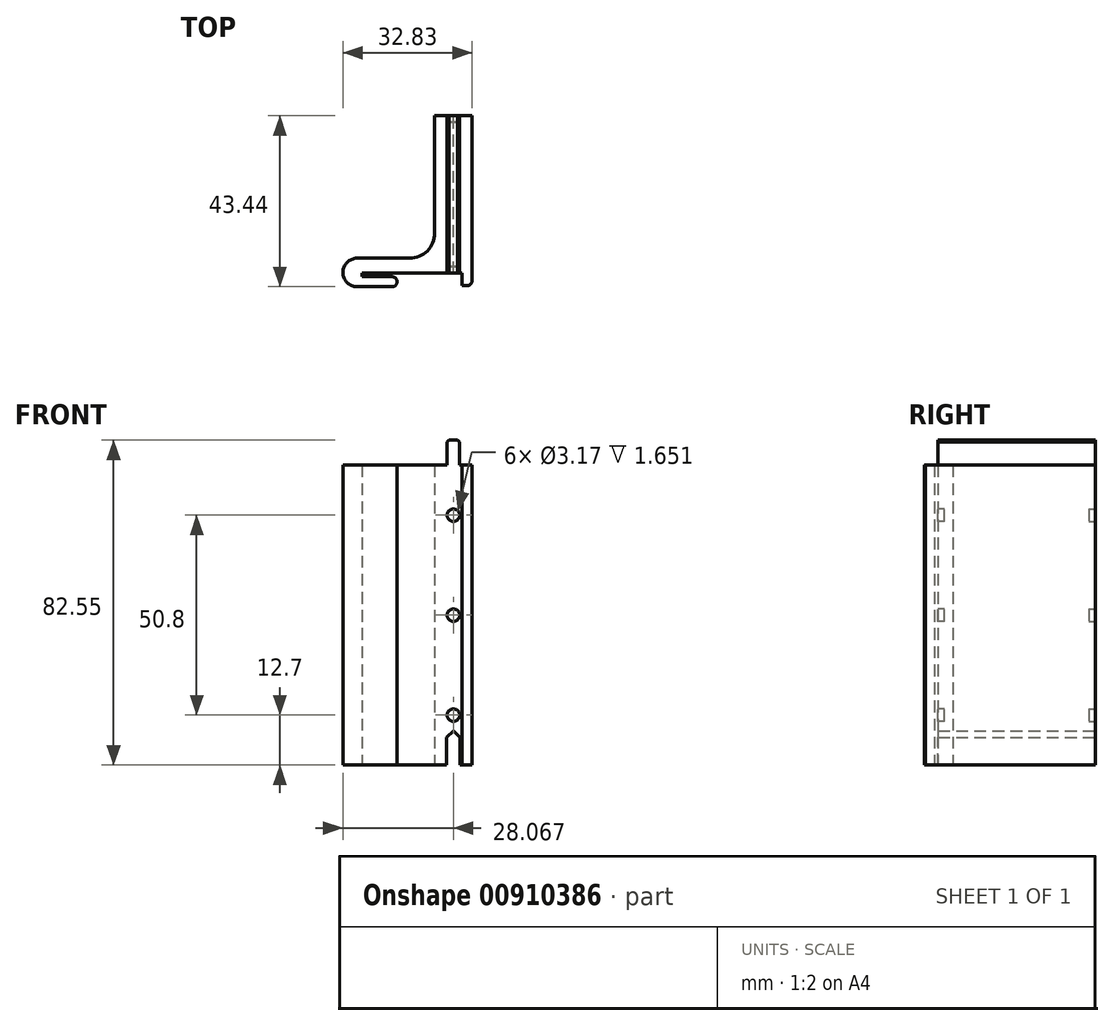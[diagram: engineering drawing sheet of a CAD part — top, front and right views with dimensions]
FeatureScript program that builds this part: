
annotation { "Feature Type Name" : "Feature", "Feature Type Description" : "" }
export const myFeature = defineFeature(function(context is Context, id is Id, definition is map)
    precondition{}
    {
        {
            var Q0;
            Q0=qCreatedBy(makeId("Top.planeOp"),FACE);
            var sketch = newSketch(context, id + "F0", { "sketchPlane" : qUnion([Q0])});
            skLineSegment(sketch, "E0", {"start": v(-6.99, 40) * mm, "end": v(-6.99, 10.16) * mm});
            skLineSegment(sketch, "E1", {"start": v(-13.34, 3.8) * mm, "end": v(-26.67, 3.8) * mm});
            skLineSegment(sketch, "E2", {"start": v(-26.67, -3.43) * mm, "end": v(-17.78, -3.43) * mm});
            skLineSegment(sketch, "E3", {"start": v(-17.78, -0.89) * mm, "end": v(-25.4, -0.89) * mm});
            skLineSegment(sketch, "E4", {"start": v(-25.4, -0.89) * mm, "end": v(-25.4, 0) * mm});
            skLineSegment(sketch, "E5", {"start": v(-25.4, 0) * mm, "end": v(0, 0) * mm});
            skLineSegment(sketch, "E6", {"start": v(0, 0) * mm, "end": v(0, -3.18) * mm});
            skLineSegment(sketch, "E7", {"start": v(0, -3.18) * mm, "end": v(1.22, -3.18) * mm});
            skLineSegment(sketch, "E8", {"start": v(2.54, -1.85) * mm, "end": v(2.54, 40) * mm});
            skLineSegment(sketch, "E9", {"start": v(2.54, 40) * mm, "end": v(-6.99, 40) * mm});
            skArc(sketch, "E10", {"start": v(-26.67, 3.8) * mm, "mid": v(-30.29, 0.2) * mm, "end": v(-26.67, -3.43) * mm});
            skPoint(sketch, "E11.visualSharp", {"position": v(-6.99, 3.81) * mm});
            skArc(sketch, "E11.filletArc", {"start": v(-13.34, 3.8) * mm, "mid": v(-8.84, 5.67) * mm, "end": v(-6.99, 10.16) * mm});
            skPoint(sketch, "E12.visualSharp", {"position": v(2.54, -3.18) * mm});
            skArc(sketch, "E12.filletArc", {"start": v(1.22, -3.18) * mm, "mid": v(2.15, -2.79) * mm, "end": v(2.54, -1.85) * mm});
            skArc(sketch, "E13", {"start": v(-17.78, -3.43) * mm, "mid": v(-16.51, -2.16) * mm, "end": v(-17.78, -0.89) * mm});
            skSolve(sketch);
        }
        {
            var Q0;
            Q0 = qSketchRegion(id + "F0", true);
            extrude(context, id + "F1", {"entities" : qUnion([Q0]), "depth" : 76.2 * mm, "offsetDistance" : 25.4 * mm});
        }
        {
            var Q0;
            Q0=makeQuery(id+"F1.opExtrude","SWEPT_FACE",FACE,{"disambiguationData":[OSD([sQuery(id+"F0.wireOp",EDGE,"E9")])]});
            var sketch = newSketch(context, id + "F2", { "sketchPlane" : qUnion([Q0])});
            skLineSegment(sketch, "E14.bottom", {"start": v(0.5, 0) * mm, "end": v(3.94, 0) * mm});
            skLineSegment(sketch, "E14.top", {"start": v(0.5, 6.99) * mm, "end": v(3.94, 6.99) * mm, "construction": true});
            skLineSegment(sketch, "E14.left", {"start": v(0.5, 0) * mm, "end": v(0.5, 6.99) * mm});
            skLineSegment(sketch, "E14.right", {"start": v(3.94, 0) * mm, "end": v(3.94, 6.99) * mm});
            skLineSegment(sketch, "E15", {"start": v(0.5, 6.99) * mm, "end": v(2.22, 8.7) * mm});
            skLineSegment(sketch, "E16", {"start": v(2.22, 8.7) * mm, "end": v(3.94, 6.99) * mm});
            skSolve(sketch);
        }
        {
            var Q0;
            Q0 = qSketchRegion(id + "F2", true);
            extrude(context, id + "F3", {"entities" : qUnion([Q0]), "operationType" : NewBodyOperationType.REMOVE, "endBound" : BoundingType.THROUGH_ALL, "oppositeDirection" : true, "depth" : 25.4 * mm, "offsetDistance" : 25.4 * mm});
        }
        {
            var Q0;
            Q0=makeQuery(id+"F1.opExtrude","SWEPT_FACE",FACE,{"disambiguationData":[OSD([sQuery(id+"F0.wireOp",EDGE,"E9")])]});
            var sketch = newSketch(context, id + "F4", { "sketchPlane" : qUnion([Q0])});
            skLineSegment(sketch, "E17.bottom", {"start": v(3.81, 76.2) * mm, "end": v(0.64, 76.2) * mm});
            skLineSegment(sketch, "E17.top", {"start": v(3.81, 82.55) * mm, "end": v(0.64, 82.55) * mm});
            skLineSegment(sketch, "E17.left", {"start": v(3.81, 76.2) * mm, "end": v(3.81, 82.55) * mm});
            skLineSegment(sketch, "E17.right", {"start": v(0.64, 76.2) * mm, "end": v(0.64, 82.55) * mm});
            skLineSegment(sketch, "E18", {"start": v(2.22, 76.2) * mm, "end": v(2.22, 8.7) * mm, "construction": true});
            skSolve(sketch);
        }
        {
            var Q0;
            Q0 = qSketchRegion(id + "F4", true);
            var Q1;
            Q1=makeQuery(id+"F1.opExtrude","SWEPT_FACE",FACE,{"disambiguationData":[OSD([sQuery(id+"F0.wireOp",EDGE,"E5")])]});
            extrude(context, id + "F5", {"entities" : qUnion([Q0]), "operationType" : NewBodyOperationType.ADD, "endBound" : BoundingType.UP_TO_SURFACE, "oppositeDirection" : true, "depth" : 25.4 * mm, "endBoundEntityFace" : qUnion([Q1]), "offsetDistance" : 25.4 * mm});
        }
        {
            var Q0;
            Q0=makeQuery(id+"F3.boolean.opBoolean","COPY",EDGE,{"derivedFrom":makeQuery(id+"F3.opExtrude","SWEPT_EDGE",EDGE,{"disambiguationData":[OSD([sQuery(id+"F0.wireOp",EDGE,"E9"),sQuery(id+"F2.wireOp",EDGE,"E14.bottom"),sQuery(id+"F2.wireOp",EDGE,"E14.right")])]})});
            var Q1;
            Q1=makeQuery(id+"F3.boolean.opBoolean","COPY",EDGE,{"derivedFrom":makeQuery(id+"F3.opExtrude","SWEPT_EDGE",EDGE,{"disambiguationData":[OSD([sQuery(id+"F0.wireOp",EDGE,"E9"),sQuery(id+"F2.wireOp",EDGE,"E14.bottom"),sQuery(id+"F2.wireOp",EDGE,"E14.left")])]})});
            var Q2;
            Q2=makeQuery(id+"F5.opExtrude","SWEPT_EDGE",EDGE,{"disambiguationData":[OSD([sQuery(id+"F4.wireOp",EDGE,"E17.top"),sQuery(id+"F4.wireOp",EDGE,"E17.right")])]});
            var Q3;
            Q3=makeQuery(id+"F5.opExtrude","SWEPT_EDGE",EDGE,{"disambiguationData":[OSD([sQuery(id+"F4.wireOp",EDGE,"E17.top"),sQuery(id+"F4.wireOp",EDGE,"E17.left")])]});
            chamfer(context, id + "F6", {"entities" : qUnion([Q0, Q1, Q2, Q3]), "width" : 0.5 * mm, "tangentPropagation" : true});
        }
        {
            var Q0;
            Q0=makeQuery(id+"F5.boolean.opBoolean","MERGE",FACE,{"derivedFrom":[makeQuery(id+"F1.opExtrude","SWEPT_FACE",FACE,{"disambiguationData":[OSD([sQuery(id+"F0.wireOp",EDGE,"E9")])]}),makeQuery(id+"F5.opExtrude","CAP_FACE",FACE,{"disambiguationData":[OSD([sQuery(id+"F4.wireOp",EDGE,"E17.bottom"),sQuery(id+"F4.wireOp",EDGE,"E17.top"),sQuery(id+"F4.wireOp",EDGE,"E17.left"),sQuery(id+"F4.wireOp",EDGE,"E17.right")])],"isStart":true})]});
            var sketch = newSketch(context, id + "F7", { "sketchPlane" : qUnion([Q0])});
            skCircle(sketch, "E19", {"center": v(2.22, 12.7) * mm, "radius": 1.59 * mm});
            skCircle(sketch, "E20", {"center": v(2.22, 38.1) * mm, "radius": 1.59 * mm});
            skCircle(sketch, "E21", {"center": v(2.22, 63.5) * mm, "radius": 1.59 * mm});
            skLineSegment(sketch, "E22", {"start": v(2.22, 0) * mm, "end": v(2.22, 12.7) * mm, "construction": true});
            skLineSegment(sketch, "E23", {"start": v(2.22, 38.1) * mm, "end": v(2.22, 12.7) * mm, "construction": true});
            skLineSegment(sketch, "E24", {"start": v(2.22, 63.5) * mm, "end": v(2.22, 38.1) * mm, "construction": true});
            skLineSegment(sketch, "E25", {"start": v(2.22, 63.5) * mm, "end": v(2.22, 76.2) * mm, "construction": true});
            skSolve(sketch);
        }
        {
            var Q0;
            Q0 = qSketchRegion(id + "F7", true);
            extrude(context, id + "F8", {"entities" : qUnion([Q0]), "operationType" : NewBodyOperationType.REMOVE, "oppositeDirection" : true, "depth" : 1.65 * mm, "offsetDistance" : 25.4 * mm});
        }
        {
            var Q0;
            Q0=makeQuery(id+"F5.boolean.opBoolean","MERGE",FACE,{"derivedFrom":[makeQuery(id+"F1.opExtrude","SWEPT_FACE",FACE,{"disambiguationData":[OSD([sQuery(id+"F0.wireOp",EDGE,"E5")])]}),makeQuery(id+"F5.opExtrude","CAP_FACE",FACE,{"disambiguationData":[OSD([sQuery(id+"F4.wireOp",EDGE,"E17.bottom"),sQuery(id+"F4.wireOp",EDGE,"E17.top"),sQuery(id+"F4.wireOp",EDGE,"E17.left"),sQuery(id+"F4.wireOp",EDGE,"E17.right")])],"isStart":false})]});
            var sketch = newSketch(context, id + "F9", { "sketchPlane" : qUnion([Q0])});
            skCircle(sketch, "E26.0.0", {"center": v(-2.22, 12.7) * mm, "radius": 1.59 * mm});
            skCircle(sketch, "E26.1.0", {"center": v(-2.22, 38.1) * mm, "radius": 1.59 * mm});
            skCircle(sketch, "E26.2.0", {"center": v(-2.22, 63.5) * mm, "radius": 1.59 * mm});
            skSolve(sketch);
        }
        {
            var Q0;
            Q0 = qSketchRegion(id + "F9", true);
            extrude(context, id + "F10", {"entities" : qUnion([Q0]), "operationType" : NewBodyOperationType.REMOVE, "oppositeDirection" : true, "depth" : 1.65 * mm, "offsetDistance" : 25.4 * mm});
        }
    });
